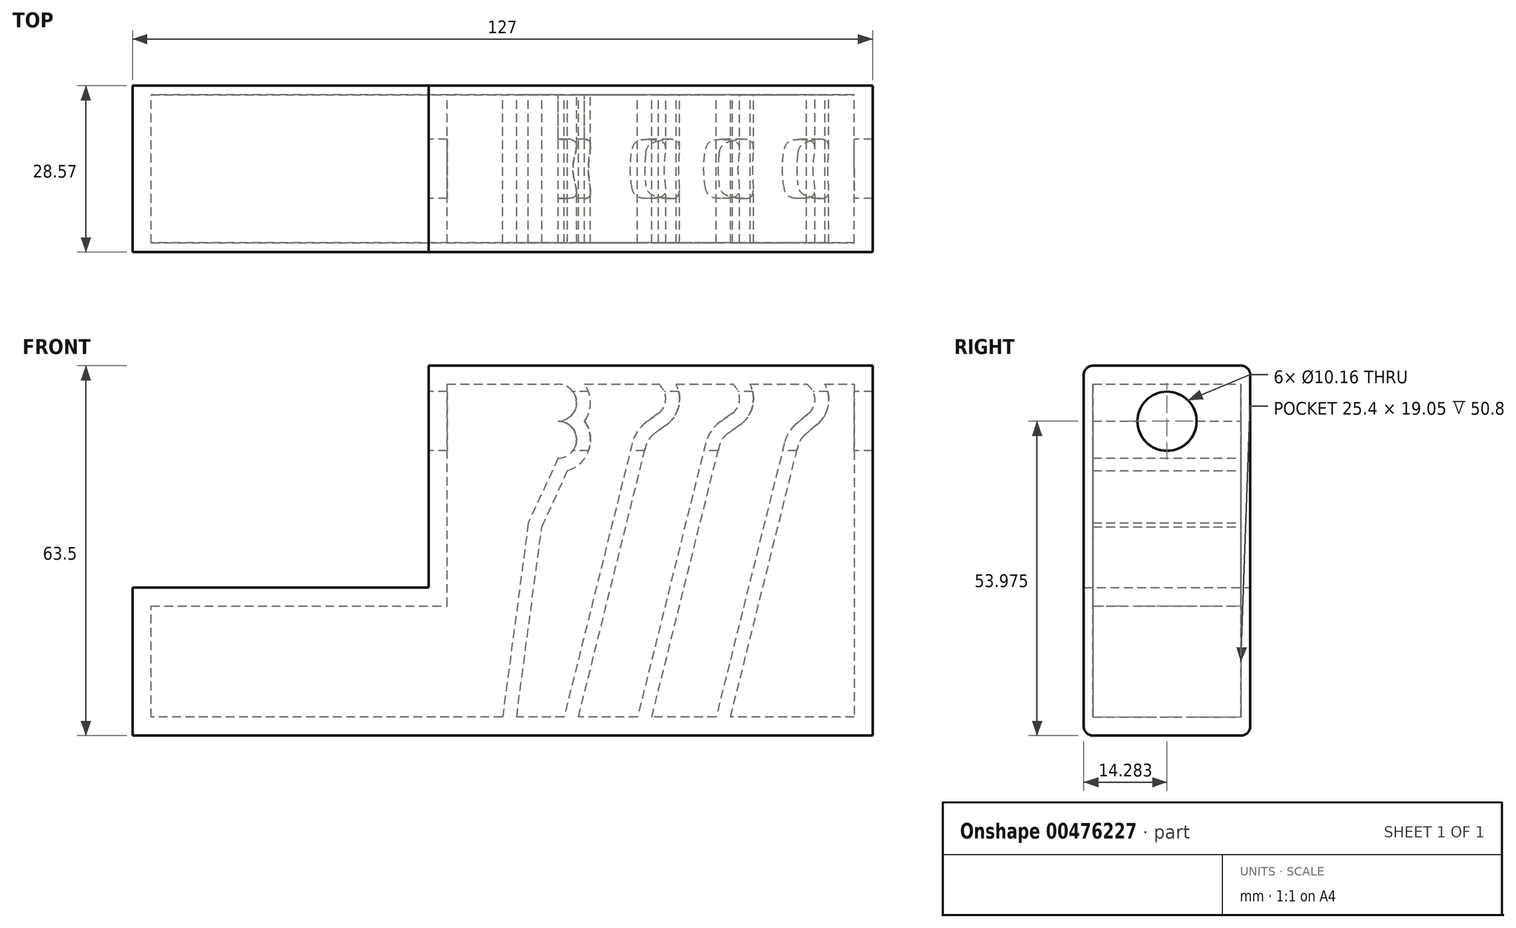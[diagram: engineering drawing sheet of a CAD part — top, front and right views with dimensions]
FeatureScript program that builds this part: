
annotation { "Feature Type Name" : "Feature", "Feature Type Description" : "" }
export const myFeature = defineFeature(function(context is Context, id is Id, definition is map)
    precondition{}
    {
        {
            var Q0;
            Q0=qCreatedBy(makeId("Front.planeOp"),FACE);
            var sketch = newSketch(context, id + "F0", { "sketchPlane" : qUnion([Q0])});
            skLineSegment(sketch, "E0", {"start": v(0, 0) * mm, "end": v(127, 0) * mm});
            skLineSegment(sketch, "E1", {"start": v(127, 0) * mm, "end": v(127, 63.5) * mm});
            skLineSegment(sketch, "E2", {"start": v(127, 63.5) * mm, "end": v(50.8, 63.5) * mm});
            skLineSegment(sketch, "E3", {"start": v(50.8, 63.5) * mm, "end": v(50.8, 25.4) * mm});
            skLineSegment(sketch, "E4", {"start": v(50.8, 25.4) * mm, "end": v(0, 25.4) * mm});
            skLineSegment(sketch, "E5", {"start": v(0, 25.4) * mm, "end": v(0, 0) * mm});
            skSolve(sketch);
        }
        {
            var Q0;
            Q0 = qSketchRegion(id + "F0", true);
            extrude(context, id + "F1", {"entities" : qUnion([Q0]), "depth" : 1.59 * mm});
        }
        {
            var Q0;
            Q0=makeQuery(id+"F1.opExtrude","CAP_FACE",FACE,{"disambiguationData":[OSD([sQuery(id+"F0.wireOp",EDGE,"E0"),sQuery(id+"F0.wireOp",EDGE,"E1"),sQuery(id+"F0.wireOp",EDGE,"E2"),sQuery(id+"F0.wireOp",EDGE,"E3"),sQuery(id+"F0.wireOp",EDGE,"E4"),sQuery(id+"F0.wireOp",EDGE,"E5")])],"isStart":false});
            var sketch = newSketch(context, id + "F2", { "sketchPlane" : qUnion([Q0])});
            skLineSegment(sketch, "E6", {"start": v(0, 0) * mm, "end": v(127, 0) * mm});
            skLineSegment(sketch, "E7", {"start": v(127, 0) * mm, "end": v(127, 63.5) * mm});
            skLineSegment(sketch, "E8", {"start": v(127, 63.5) * mm, "end": v(50.8, 63.5) * mm});
            skLineSegment(sketch, "E9", {"start": v(50.8, 63.5) * mm, "end": v(50.8, 25.4) * mm});
            skLineSegment(sketch, "E10", {"start": v(50.8, 25.4) * mm, "end": v(0, 25.4) * mm});
            skLineSegment(sketch, "E11", {"start": v(0, 25.4) * mm, "end": v(0, 0) * mm});
            skLineSegment(sketch, "E12", {"start": v(3.17, 22.22) * mm, "end": v(53.97, 22.22) * mm});
            skLineSegment(sketch, "E13", {"start": v(53.97, 22.22) * mm, "end": v(53.97, 60.33) * mm});
            skLineSegment(sketch, "E14", {"start": v(53.97, 60.33) * mm, "end": v(123.82, 60.33) * mm});
            skLineSegment(sketch, "E15", {"start": v(123.82, 60.33) * mm, "end": v(123.82, 3.18) * mm});
            skLineSegment(sketch, "E16", {"start": v(123.82, 3.18) * mm, "end": v(3.18, 3.17) * mm});
            skLineSegment(sketch, "E17", {"start": v(3.18, 3.17) * mm, "end": v(3.17, 22.22) * mm});
            skPoint(sketch, "E18", {"position": v(73.03, 53.97) * mm});
            skArc(sketch, "E19", {"start": v(73.02, 53.97) * mm, "mid": v(76.2, 57.15) * mm, "end": v(73.02, 60.32) * mm});
            skPoint(sketch, "E20", {"position": v(73.03, 47.62) * mm});
            skArc(sketch, "E21", {"start": v(73.03, 47.62) * mm, "mid": v(76.2, 50.8) * mm, "end": v(73.03, 53.97) * mm});
            skLineSegment(sketch, "E22", {"start": v(73.03, 47.62) * mm, "end": v(67.93, 36.51) * mm});
            skLineSegment(sketch, "E23", {"start": v(67.93, 36.51) * mm, "end": v(63.5, 3.17) * mm});
            skLineSegment(sketch, "E24", {"start": v(65.9, 3.17) * mm, "end": v(70.24, 35.84) * mm});
            skLineSegment(sketch, "E25", {"start": v(70.24, 35.84) * mm, "end": v(74.67, 45.5) * mm});
            skArc(sketch, "E26", {"start": v(74.67, 45.5) * mm, "mid": v(78.28, 49) * mm, "end": v(77.58, 53.97) * mm});
            skArc(sketch, "E27", {"start": v(77.58, 53.97) * mm, "mid": v(78.58, 57.15) * mm, "end": v(77.58, 60.33) * mm});
            skArc(sketch, "E28", {"start": v(90.17, 55.24) * mm, "mid": v(91.5, 57.76) * mm, "end": v(90.28, 60.33) * mm});
            skLineSegment(sketch, "E29", {"start": v(90.17, 55.24) * mm, "end": v(88.23, 53.86) * mm});
            skArc(sketch, "E30", {"start": v(88.23, 53.86) * mm, "mid": v(86.67, 52.26) * mm, "end": v(85.76, 50.22) * mm});
            skLineSegment(sketch, "E31", {"start": v(85.76, 50.22) * mm, "end": v(74.06, 3.17) * mm});
            skLineSegment(sketch, "E32", {"start": v(76.51, 3.17) * mm, "end": v(88.07, 49.65) * mm});
            skArc(sketch, "E33", {"start": v(93.29, 60.33) * mm, "mid": v(93.72, 56.5) * mm, "end": v(91.56, 53.3) * mm});
            skLineSegment(sketch, "E34", {"start": v(91.56, 53.3) * mm, "end": v(89.62, 51.92) * mm});
            skArc(sketch, "E35", {"start": v(89.62, 51.92) * mm, "mid": v(88.64, 50.92) * mm, "end": v(88.07, 49.65) * mm});
            skPoint(sketch, "E36", {"position": v(102.98, 60.33) * mm});
            skArc(sketch, "E37", {"start": v(102.82, 55.25) * mm, "mid": v(104.17, 57.74) * mm, "end": v(102.98, 60.33) * mm});
            skLineSegment(sketch, "E38", {"start": v(102.82, 55.25) * mm, "end": v(100.89, 53.9) * mm});
            skArc(sketch, "E39", {"start": v(100.89, 53.9) * mm, "mid": v(99.3, 52.3) * mm, "end": v(98.36, 50.22) * mm});
            skLineSegment(sketch, "E40", {"start": v(98.36, 50.22) * mm, "end": v(86.66, 3.18) * mm});
            skLineSegment(sketch, "E41", {"start": v(89.11, 3.17) * mm, "end": v(100.67, 49.65) * mm});
            skArc(sketch, "E42", {"start": v(105.97, 60.33) * mm, "mid": v(106.38, 56.48) * mm, "end": v(104.18, 53.3) * mm});
            skLineSegment(sketch, "E43", {"start": v(104.18, 53.3) * mm, "end": v(102.25, 51.95) * mm});
            skArc(sketch, "E44", {"start": v(102.25, 51.95) * mm, "mid": v(101.25, 50.94) * mm, "end": v(100.67, 49.65) * mm});
            skPoint(sketch, "E45", {"position": v(115.68, 60.33) * mm});
            skArc(sketch, "E46", {"start": v(115.97, 55.25) * mm, "mid": v(117.1, 57.86) * mm, "end": v(115.68, 60.33) * mm});
            skLineSegment(sketch, "E47", {"start": v(115.97, 55.25) * mm, "end": v(113.95, 53.56) * mm});
            skArc(sketch, "E48", {"start": v(113.95, 53.56) * mm, "mid": v(112.64, 52.06) * mm, "end": v(111.87, 50.22) * mm});
            skLineSegment(sketch, "E49", {"start": v(111.87, 50.22) * mm, "end": v(100.16, 3.18) * mm});
            skLineSegment(sketch, "E50", {"start": v(102.62, 3.17) * mm, "end": v(114.18, 49.65) * mm});
            skArc(sketch, "E51", {"start": v(118.81, 60.33) * mm, "mid": v(119.39, 56.64) * mm, "end": v(117.5, 53.42) * mm});
            skLineSegment(sketch, "E52", {"start": v(117.5, 53.42) * mm, "end": v(115.48, 51.74) * mm});
            skArc(sketch, "E53", {"start": v(115.48, 51.74) * mm, "mid": v(114.66, 50.8) * mm, "end": v(114.18, 49.65) * mm});
            skSolve(sketch);
        }
        {
            var Q0;
            Q0 = qSketchRegion(id + "F2", true);
            var Q1;
            {var subQ0=sQuery(id+"F2.wireOp",EDGE,"E19");Q1=makeQuery(id+"F2.imprint","IMPRINT",FACE,{"disambiguationData":[TD([[makeQuery(id+"F2.imprint","IMPRINT",EDGE,{"derivedFrom":subQ0}),-1.0]])]});}
            var Q2;
            {var subQ3=sQuery(id+"F2.wireOp",EDGE,"E28");Q2=makeQuery(id+"F2.imprint","IMPRINT",FACE,{"disambiguationData":[TD([[makeQuery(id+"F2.imprint","IMPRINT",EDGE,{"derivedFrom":subQ3}),-1.0]])]});}
            var Q3;
            {var subQ0=sQuery(id+"F2.wireOp",EDGE,"E37");Q3=makeQuery(id+"F2.imprint","IMPRINT",FACE,{"disambiguationData":[TD([[makeQuery(id+"F2.imprint","IMPRINT",EDGE,{"derivedFrom":subQ0}),-1.0]])]});}
            var Q4;
            {var subQ0=sQuery(id+"F2.wireOp",EDGE,"E46");Q4=makeQuery(id+"F2.imprint","IMPRINT",FACE,{"disambiguationData":[TD([[makeQuery(id+"F2.imprint","IMPRINT",EDGE,{"derivedFrom":subQ0}),-1.0]])]});}
            extrude(context, id + "F3", {"entities" : qUnion([Q0, Q1, Q2, Q3, Q4]), "operationType" : NewBodyOperationType.ADD, "depth" : 25.4 * mm});
        }
        {
            var Q0;
            Q0=makeQuery(id+"F3.boolean.opBoolean","MERGE",FACE,{"derivedFrom":[makeQuery(id+"F1.opExtrude","SWEPT_FACE",FACE,{"disambiguationData":[OSD([sQuery(id+"F0.wireOp",EDGE,"E3")])]}),makeQuery(id+"F3.opExtrude","SWEPT_FACE",FACE,{"disambiguationData":[OSD([sQuery(id+"F2.wireOp",EDGE,"E9")])]})]});
            var sketch = newSketch(context, id + "F4", { "sketchPlane" : qUnion([Q0])});
            skCircle(sketch, "E54", {"center": v(14.29, 53.98) * mm, "radius": 5.08 * mm});
            skSolve(sketch);
        }
        {
            var Q0;
            Q0 = qSketchRegion(id + "F4", true);
            extrude(context, id + "F5", {"entities" : qUnion([Q0]), "operationType" : NewBodyOperationType.REMOVE, "endBound" : BoundingType.THROUGH_ALL, "oppositeDirection" : true, "depth" : 25.4 * mm});
        }
        {
            var Q0;
            Q0=makeQuery(id+"F3.opExtrude","CAP_FACE",FACE,{"disambiguationData":[OSD([sQuery(id+"F2.wireOp",EDGE,"E6"),sQuery(id+"F2.wireOp",EDGE,"E7"),sQuery(id+"F2.wireOp",EDGE,"E8"),sQuery(id+"F2.wireOp",EDGE,"E9"),sQuery(id+"F2.wireOp",EDGE,"E10"),sQuery(id+"F2.wireOp",EDGE,"E11"),sQuery(id+"F2.wireOp",EDGE,"E12"),sQuery(id+"F2.wireOp",EDGE,"E13"),sQuery(id+"F2.wireOp",EDGE,"E14"),sQuery(id+"F2.wireOp",EDGE,"E15"),sQuery(id+"F2.wireOp",EDGE,"E16"),sQuery(id+"F2.wireOp",EDGE,"E17"),sQuery(id+"F2.wireOp",EDGE,"E19"),sQuery(id+"F2.wireOp",EDGE,"E21"),sQuery(id+"F2.wireOp",EDGE,"E22"),sQuery(id+"F2.wireOp",EDGE,"E23"),sQuery(id+"F2.wireOp",EDGE,"E24"),sQuery(id+"F2.wireOp",EDGE,"E25"),sQuery(id+"F2.wireOp",EDGE,"E26"),sQuery(id+"F2.wireOp",EDGE,"E27"),sQuery(id+"F2.wireOp",EDGE,"E28"),sQuery(id+"F2.wireOp",EDGE,"E29"),sQuery(id+"F2.wireOp",EDGE,"E30"),sQuery(id+"F2.wireOp",EDGE,"E31"),sQuery(id+"F2.wireOp",EDGE,"E32"),sQuery(id+"F2.wireOp",EDGE,"E33"),sQuery(id+"F2.wireOp",EDGE,"E34"),sQuery(id+"F2.wireOp",EDGE,"E35"),sQuery(id+"F2.wireOp",EDGE,"E37"),sQuery(id+"F2.wireOp",EDGE,"E38"),sQuery(id+"F2.wireOp",EDGE,"E39"),sQuery(id+"F2.wireOp",EDGE,"E40"),sQuery(id+"F2.wireOp",EDGE,"E41"),sQuery(id+"F2.wireOp",EDGE,"E42"),sQuery(id+"F2.wireOp",EDGE,"E43"),sQuery(id+"F2.wireOp",EDGE,"E44"),sQuery(id+"F2.wireOp",EDGE,"E46"),sQuery(id+"F2.wireOp",EDGE,"E47"),sQuery(id+"F2.wireOp",EDGE,"E48"),sQuery(id+"F2.wireOp",EDGE,"E49"),sQuery(id+"F2.wireOp",EDGE,"E50"),sQuery(id+"F2.wireOp",EDGE,"E51"),sQuery(id+"F2.wireOp",EDGE,"E52"),sQuery(id+"F2.wireOp",EDGE,"E53")])],"isStart":false});
            var sketch = newSketch(context, id + "F6", { "sketchPlane" : qUnion([Q0])});
            skLineSegment(sketch, "E55", {"start": v(0, 0) * mm, "end": v(0, 25.4) * mm});
            skLineSegment(sketch, "E56", {"start": v(0, 25.4) * mm, "end": v(50.8, 25.4) * mm});
            skLineSegment(sketch, "E57", {"start": v(50.8, 25.4) * mm, "end": v(50.8, 63.5) * mm});
            skLineSegment(sketch, "E58", {"start": v(50.8, 63.5) * mm, "end": v(127, 63.5) * mm});
            skLineSegment(sketch, "E59", {"start": v(127, 63.5) * mm, "end": v(127, 0) * mm});
            skLineSegment(sketch, "E60", {"start": v(127, 0) * mm, "end": v(0, 0) * mm});
            skSolve(sketch);
        }
        {
            var Q0;
            Q0 = qSketchRegion(id + "F6", true);
            extrude(context, id + "F7", {"entities" : qUnion([Q0]), "operationType" : NewBodyOperationType.ADD, "depth" : 1.59 * mm});
        }
        {
            var Q0;
            Q0=makeQuery(id+"F7.opExtrude","CAP_EDGE",EDGE,{"disambiguationData":[OSD([sQuery(id+"F6.wireOp",EDGE,"E58")])],"isStart":false});
            var Q1;
            Q1=makeQuery(id+"F1.opExtrude","CAP_EDGE",EDGE,{"disambiguationData":[OSD([sQuery(id+"F0.wireOp",EDGE,"E2")])],"isStart":true});
            var Q2;
            Q2=makeQuery(id+"F7.opExtrude","CAP_EDGE",EDGE,{"disambiguationData":[OSD([sQuery(id+"F6.wireOp",EDGE,"E60")])],"isStart":false});
            var Q3;
            Q3=makeQuery(id+"F1.opExtrude","CAP_EDGE",EDGE,{"disambiguationData":[OSD([sQuery(id+"F0.wireOp",EDGE,"E0")])],"isStart":true});
            fillet(context, id + "F8", {"entities" : qUnion([Q0, Q1, Q2, Q3]), "radius" : 1.59 * mm, "tangentPropagation" : true, "allowEdgeOverflow" : false});
        }
    });
